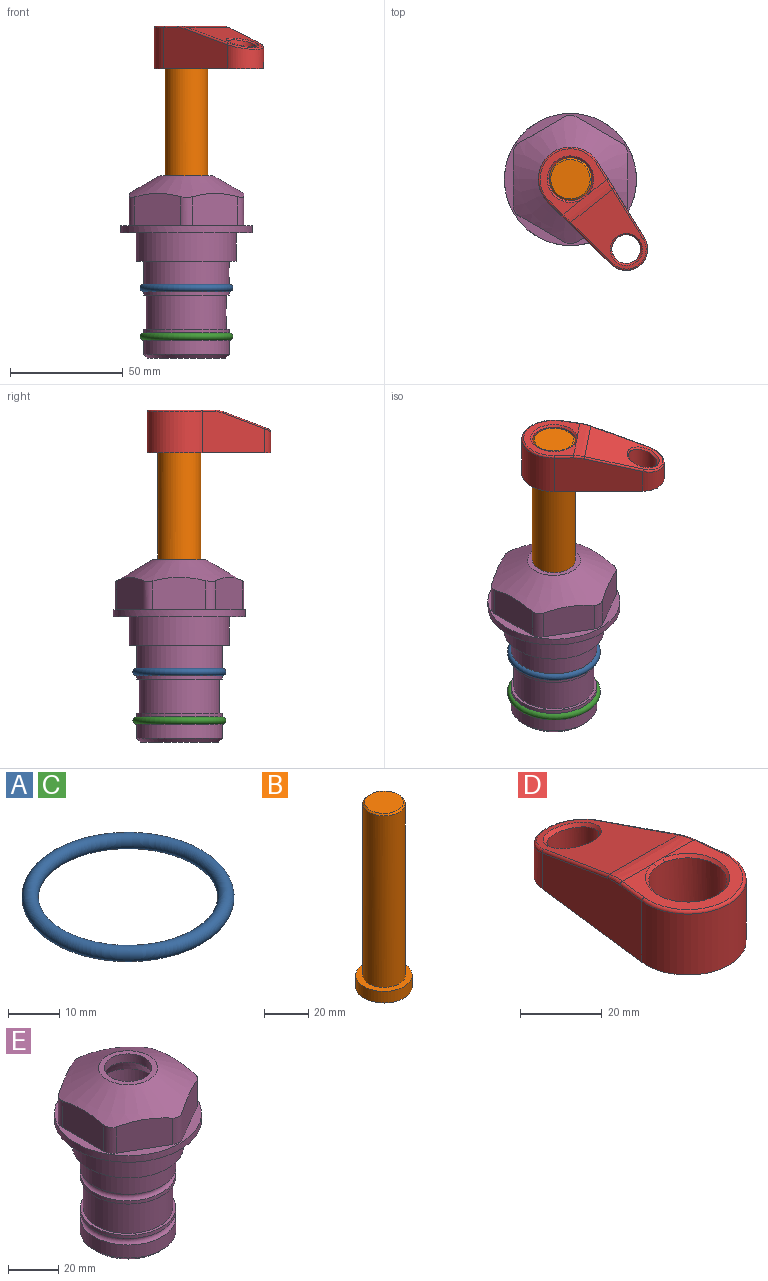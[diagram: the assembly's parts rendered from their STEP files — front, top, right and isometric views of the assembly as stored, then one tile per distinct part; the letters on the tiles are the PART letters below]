
ASSEMBLY  parts=5 mates=4
PART A: 1 faces, bbox 44.7x44.7x3.2 mm
  f0: torus R=19.05mm, axis (0,0,1), area 1193.9mm2
PART B: 6 faces, bbox 25.4x25.4x101.6 mm
  f0: plane 17.46x17.46mm, normal (0,0,1), area 239.5mm2, adj f5
  f1: plane 25.4x25.4mm, normal (0,0,-1), area 506.7mm2, adj f2
  f2: cylinder r=12.7mm len=25.4mm, axis (0,0,1), area 506.7mm2, adj f1,f3
  f3: plane 25.4x25.4mm, normal (0,0,1), area 221.7mm2, adj f2,f4
  f4: cylinder r=9.53mm len=94.46mm, axis (0,0,1), area 5653mm2, adj f3,f5
  f5: cone r=8.73mm half-angle=45deg, axis (0,0,-1), area 64.4mm2, adj f0,f4
PART C: same geometry as A
PART D: 31 faces, bbox 31.7x65.5x19.8 mm
  f0: plane 39.12x18.26mm, normal (0.99,0.12,0), area 612.2mm2, adj f1,f4,f7,f11,f13,f15
  f1: cylinder r=9.53mm len=18.91mm, axis (0,0,-1), area 296.1mm2, adj f0,f2,f7,f17
  f2: plane 39.12x18.26mm, normal (-0.99,0.12,0), area 612.2mm2, adj f1,f4,f7,f12,f14,f16
  f3: cylinder r=6.35mm len=12.7mm, axis (0,0,-1), area 362.4mm2, adj f7,f18
  f4: cylinder r=14.29mm len=28.58mm, axis (0,0,-1), area 882.2mm2, adj f0,f2,f7,f10
  f5: cylinder r=9.53mm len=19.05mm, axis (0,0,-1), area 1092.6mm2, adj f7,f19,f20
  f6: plane 26.99x23.69mm, normal (0,0,1), area 216.2mm2, adj f9,f10,f11,f12,f19
  f7: plane 63.5x28.58mm, normal (0,0,-1), area 661.8mm2, adj f0,f1,f2,f3,f4,f5,f22,f23
  f8: plane 33.52x23.6mm, normal (0,0.26,0.97), area 486mm2, adj f9,f15,f16,f17,f18
  f9: cylinder r=19.05mm len=24.72mm, axis (1,0,0), area 120.4mm2, adj f6,f8,f13,f14,f20
  f10: torus R=13.49mm, axis (0,0,1), area 59mm2, adj f4,f6,f11,f12
  f11: cylinder r=0.79mm len=8.67mm, axis (0.12,-0.99,0), area 10.8mm2, adj f0,f6,f10,f13
  f12: cylinder r=0.79mm len=8.67mm, axis (0.12,0.99,0), area 10.8mm2, adj f2,f6,f10,f14
  f13: bspline ~4.95x1.42mm, area 6.1mm2, adj f0,f9,f11,f15
  f14: bspline ~4.95x1.42mm, area 6.1mm2, adj f2,f9,f12,f16
  f15: cylinder r=0.79mm len=25.95mm, axis (0.12,-0.96,0.26), area 32.9mm2, adj f0,f8,f13,f17
  f16: cylinder r=0.79mm len=25.95mm, axis (0.12,0.96,-0.26), area 32.9mm2, adj f2,f8,f14,f17
  f17: bspline ~18.91x8.38mm, area 30mm2, adj f1,f8,f15,f16
  f18: bspline ~14.29x14.29mm, area 48.3mm2, adj f3,f8
  f19: cone r=9.53mm half-angle=45deg, axis (0,0,1), area 66.5mm2, adj f5,f6,f20
  f20: bspline ~3.22x0.96mm, area 3.5mm2, adj f5,f9,f19
  f21: plane 2.75x2.72mm, normal (0,0,-1), area 2.9mm2, adj f23,f25,f28
  f22: plane 23.05x15.88mm, normal (-0.99,-0.12,0), area 323.6mm2, adj f7,f25,f26,f27,f28,f29
  f23: plane 23.05x15.88mm, normal (0.99,-0.12,0), area 323.6mm2, adj f7,f21,f25,f27,f28,f30
  f24: cylinder r=9.53mm len=10.69mm, axis (0,0,-1), area 114.7mm2, adj f7,f27,f29,f30
  f25: cylinder r=12.7mm len=20.59mm, axis (0,0,-1), area 381.1mm2, adj f7,f21,f22,f23,f26,f28
  f26: plane 2.75x2.72mm, normal (0,0,-1), area 2.9mm2, adj f22,f25,f28
  f27: plane 19.72x18.37mm, normal (0,-0.26,-0.97), area 291.8mm2, adj f22,f23,f24,f28,f29,f30
  f28: cylinder r=15.88mm len=19.92mm, axis (1,0,0), area 54.8mm2, adj f21,f22,f23,f25,f26,f27
  f29: cylinder r=1.59mm len=11mm, axis (0,0,-1), area 34.7mm2, adj f7,f22,f24,f27
  f30: cylinder r=1.59mm len=11mm, axis (0,0,-1), area 34.7mm2, adj f7,f23,f24,f27
PART E: 36 faces, bbox 58.7x58.7x81 mm
  f0: cylinder r=17.78mm len=35.56mm, axis (0,0,1), area 1670.8mm2, adj f23,f24,f31
  f1: cylinder r=19.05mm len=38.1mm, axis (0,0,1), area 1191.9mm2, adj f26,f27,f30
  f2: plane 58.66x58.66mm, normal (0,0,-1), area 1150.6mm2, adj f3,f28
  f3: cylinder r=29.33mm len=58.66mm, axis (0,0,-1), area 585.1mm2, adj f2,f4
  f4: plane 58.66x58.66mm, normal (0,0,1), area 475.9mm2, adj f3,f5,f6,f7,f8,f9,f10,f11
  f5: plane 20.32x14.34mm, normal (-0.5,0.87,0), area 324.4mm2, adj f4,f15,f16,f17
  f6: plane 20.32x14.34mm, normal (0.5,0.87,0), area 324.4mm2, adj f4,f14,f15,f17
  f7: plane 23.48x14.34mm, normal (1,0,0), area 324.4mm2, adj f4,f13,f14,f17
  f8: plane 20.32x14.34mm, normal (0.5,-0.87,0), area 324.4mm2, adj f4,f12,f13,f17
  f9: plane 20.32x14.34mm, normal (-0.5,-0.87,0), area 324.4mm2, adj f4,f11,f12,f17
  f10: plane 23.48x14.34mm, normal (-1,0,0), area 324.4mm2, adj f4,f11,f16,f17
  f11: cylinder r=5.08mm len=12.85mm, axis (0,0,-1), area 67.2mm2, adj f4,f9,f10,f17
  f12: cylinder r=5.08mm len=12.85mm, axis (0,0,-1), area 67.2mm2, adj f4,f8,f9,f17
  f13: cylinder r=5.08mm len=12.85mm, axis (0,0,-1), area 67.2mm2, adj f4,f7,f8,f17
  f14: cylinder r=5.08mm len=12.85mm, axis (0,0,-1), area 67.2mm2, adj f4,f6,f7,f17
  f15: cylinder r=5.08mm len=12.85mm, axis (0,0,-1), area 67.2mm2, adj f4,f5,f6,f17
  f16: cylinder r=5.08mm len=12.85mm, axis (0,0,-1), area 67.2mm2, adj f4,f5,f10,f17
  f17: cone r=11.73mm half-angle=60deg, axis (0,0,-1), area 2071.8mm2, adj f5,f6,f7,f8,f9,f10,f11,f12
  f18: plane 23.46x23.46mm, normal (0,0,1), area 147.4mm2, adj f17,f35
  f19: plane 34.93x34.93mm, normal (0,0,-1), area 958mm2, adj f29
  f20: cylinder r=19.05mm len=38.1mm, axis (0,0,1), area 760.1mm2, adj f21,f29
  f21: torus R=19.05mm, axis (0,0,1), area 565.3mm2, adj f20,f22
  f22: cylinder r=19.05mm len=38.1mm, axis (0,0,1), area 190mm2, adj f21,f23
  f23: plane 38.1x38.1mm, normal (0,0,1), area 146.9mm2, adj f0,f22
  f24: plane 38.1x38.1mm, normal (0,0,-1), area 146.9mm2, adj f0,f25
  f25: cylinder r=19.05mm len=38.1mm, axis (0,0,1), area 190mm2, adj f24,f26
  f26: torus R=19.05mm, axis (0,0,1), area 565.3mm2, adj f1,f25
  f27: plane 44.45x44.45mm, normal (0,0,-1), area 411.7mm2, adj f1,f28
  f28: cylinder r=22.23mm len=44.45mm, axis (0,0,1), area 1773.5mm2, adj f2,f27
  f29: cone r=19.05mm half-angle=45deg, axis (0,0,1), area 257.5mm2, adj f19,f20
  f30: cylinder r=3.17mm len=6.75mm, axis (-1,0,0), area 128mm2, adj f1,f33
  f31: cylinder r=3.17mm len=6.35mm, axis (-1,0,0), area 102.5mm2, adj f0,f33
  f32: plane 25.4x25.4mm, normal (0,0,1), area 506.7mm2, adj f33
  f33: cylinder r=12.7mm len=66.42mm, axis (0,0,-1), area 5236.2mm2, adj f30,f31,f32,f34
  f34: cone r=9.53mm half-angle=30deg, axis (0,0,-1), area 443.4mm2, adj f33,f35
  f35: cylinder r=9.53mm len=19.05mm, axis (0,0,-1), area 240.9mm2, adj f18,f34
PLACE A at identity
PLACE B rot(axis=(0,0,-1),141.4deg) t=(0,0,27.55)mm
PLACE C t=(0,0,-21.59)mm
PLACE D rot(axis=(0,0,-1),141.4deg) t=(0,0,28.35)mm
PLACE E at identity fixed
MATE fastened E.f0 <-> C.f0  axis (0,0,1) through (0,0,-46.1)mm
MATE fastened B.f2 <-> D.f4  axis (0,0,1) through (0,0,91.05)mm
MATE cylindrical E.f0 <-> B.f2  axis (0,0,1) through (0,0,-50.55)mm
MATE fastened E.f0 <-> A.f0  axis (0,0,1) through (0,0,-24.51)mm
